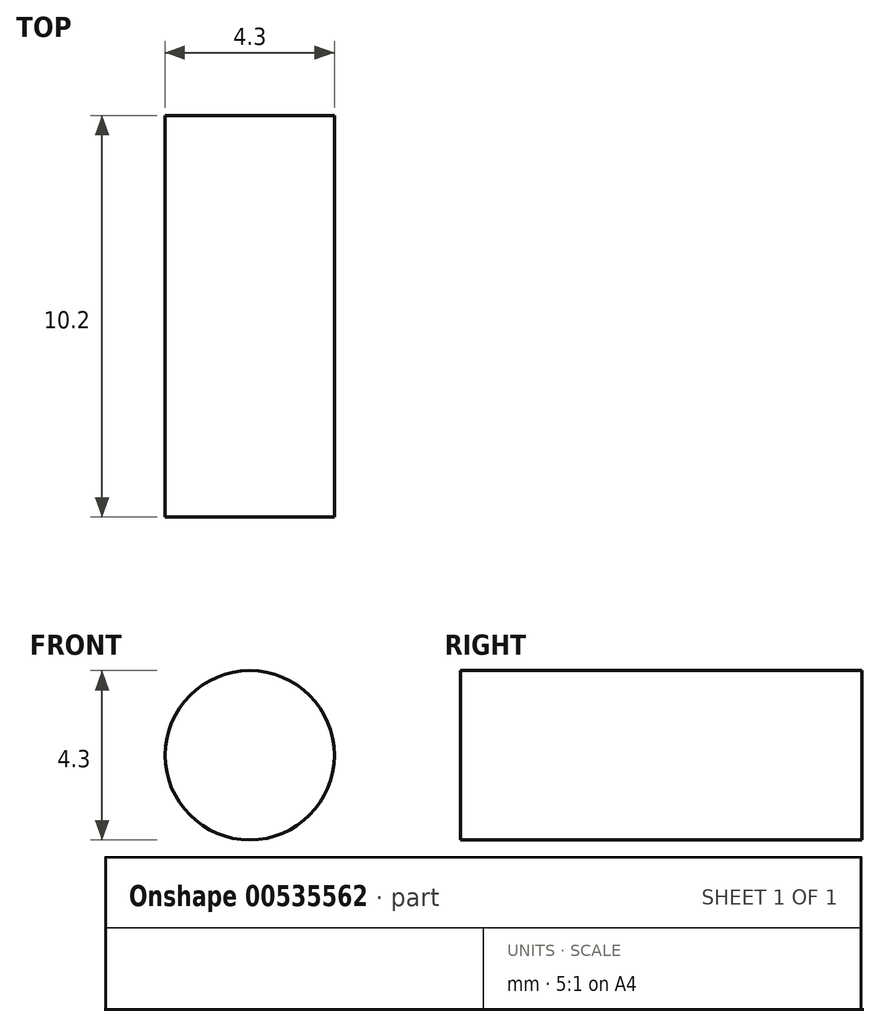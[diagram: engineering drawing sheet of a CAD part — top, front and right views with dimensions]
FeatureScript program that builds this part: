
annotation { "Feature Type Name" : "Feature", "Feature Type Description" : "" }
export const myFeature = defineFeature(function(context is Context, id is Id, definition is map)
    precondition{}
    {
        {
            var Q0;
            Q0=qCreatedBy(makeId("Front.planeOp"),FACE);
            var sketch = newSketch(context, id + "F0", { "sketchPlane" : qUnion([Q0])});
            skCircle(sketch, "E0", {"center": v(0, 0) * mm, "radius": 2.15 * mm});
            skSolve(sketch);
        }
        {
            var Q0;
            Q0 = qSketchRegion(id + "F0", true);
            extrude(context, id + "F1", {"entities" : qUnion([Q0]), "depth" : 10.2 * mm, "offsetDistance" : 25 * mm, "symmetric" : true});
        }
    });
